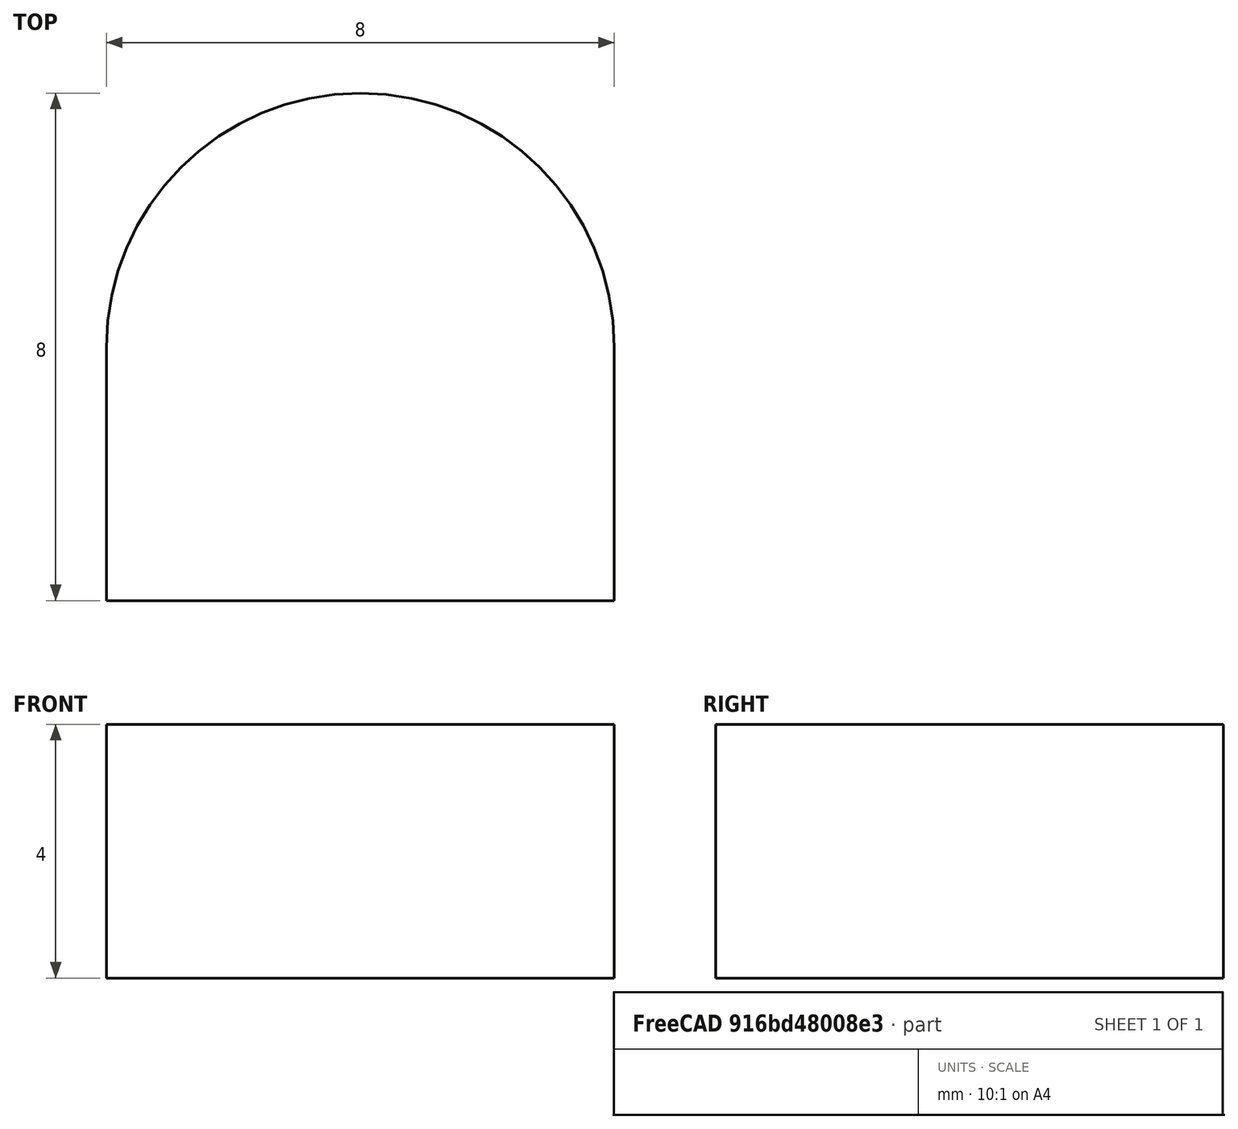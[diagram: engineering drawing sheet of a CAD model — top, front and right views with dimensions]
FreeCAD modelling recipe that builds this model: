
FCSTD DOCUMENT  (FreeCAD 0.19R)
Label: dry box spacer 4mm
License: All rights reserved
LicenseURL: http://en.wikipedia.org/wiki/All_rights_reserved
objects: Sketcher::SketchObject×1, PartDesign::Pad×1, PartDesign::Body×1
note: 4 computed .brp shape members not serialized (recipe doc carries the construction recipe); baked Part::Feature solids carry a one-line shape summary decoded from their .brp

FEATURE [Sketcher::SketchObject] Sketch
  FullyConstrained = true
  MapMode = 5
  Support = -> [XY_Plane]
  sketch-geometry (4):
    g0: LineSegment StartX=0 StartY=0 StartZ=0 EndX=8 EndY=0 EndZ=0
    g1: LineSegment StartX=8 StartY=0 StartZ=0 EndX=8 EndY=4 EndZ=0
    g2: LineSegment StartX=0 StartY=0 StartZ=0 EndX=0 EndY=4 EndZ=0
    g3: ArcOfCircle CenterX=4 CenterY=4 CenterZ=0 NormalX=0 NormalY=0 NormalZ=1 AngleXU=0 Radius=4 StartAngle=0 EndAngle=3.14159
  constraints (12):
    c: Coincident(g0,g-1)
    c: PointOnObject(g0,g-1)
    c: Coincident(g1,g0)
    c: Vertical(g1)
    c: Coincident(g2,g0)
    c: PointOnObject(g2,g-2)
    c: Horizontal(g1,g2)
    c: Coincident(g3,g2)
    c: Coincident(g3,g1)
    c: Horizontal(g3,g2)
    c: DistanceX(g0,g0) = 8
    c: DistanceY(g1,g1) = 4
FEATURE [PartDesign::Pad] Pad
  Direction = (1,1,1)
  Length = 4
  Length2 = 100
  Profile = -> Sketch
  Type = 0
FEATURE [PartDesign::Body] Body
  Group = -> [Sketch,Pad]
  Origin = -> Origin
  Tip = -> Pad
